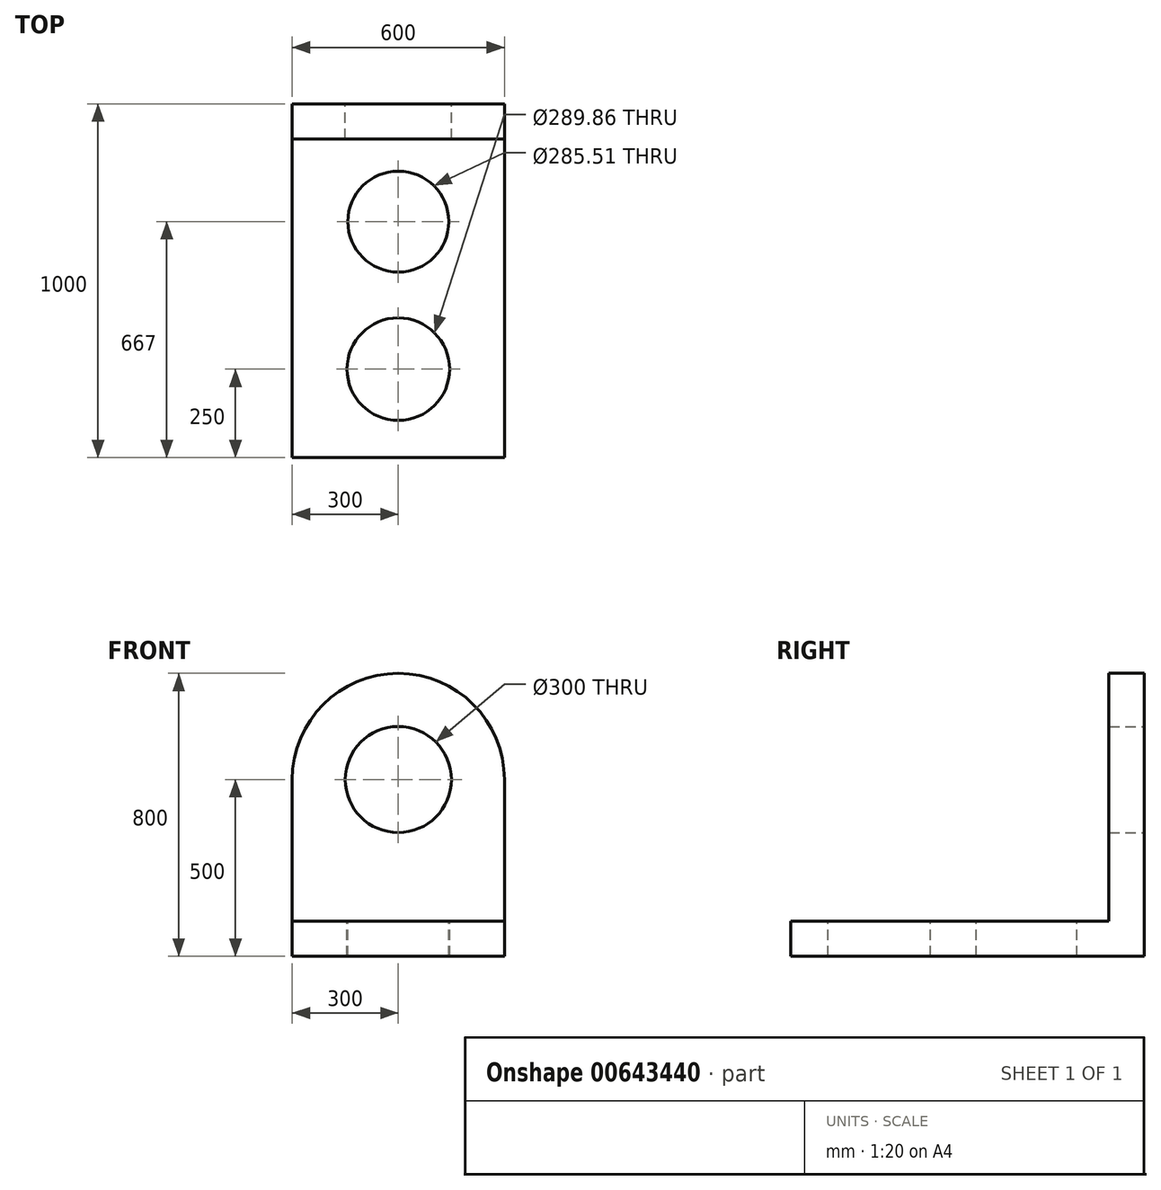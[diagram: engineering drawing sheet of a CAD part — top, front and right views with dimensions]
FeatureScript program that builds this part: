
annotation { "Feature Type Name" : "Feature", "Feature Type Description" : "" }
export const myFeature = defineFeature(function(context is Context, id is Id, definition is map)
    precondition{}
    {
        {
            var Q0;
            Q0=qCreatedBy(makeId("Front.planeOp"),FACE);
            var sketch = newSketch(context, id + "F0", { "sketchPlane" : qUnion([Q0])});
            skCircle(sketch, "E0", {"center": v(0, 0) * mm, "radius": 150 * mm});
            skArc(sketch, "E1", {"start": v(300, 0) * mm, "mid": v(0, 300) * mm, "end": v(-300, 0) * mm});
            skLineSegment(sketch, "E2", {"start": v(-300, 0) * mm, "end": v(-300, -500) * mm});
            skLineSegment(sketch, "E3", {"start": v(300, 0) * mm, "end": v(300, -500) * mm});
            skLineSegment(sketch, "E4", {"start": v(300, -500) * mm, "end": v(-300, -500) * mm});
            skLineSegment(sketch, "E5", {"start": v(-300, -400) * mm, "end": v(300, -400) * mm});
            skSolve(sketch);
        }
        {
            var Q0;
            Q0=makeQuery(id+"F0.imprint","IMPRINT",FACE,{"disambiguationData":[TD([[makeQuery(id+"F0.imprint","IMPRINT",EDGE,{"derivedFrom":sQuery(id+"F0.wireOp",EDGE,"E0")}),-1.0]])]});
            extrude(context, id + "F1", {"entities" : qUnion([Q0]), "depth" : 100 * mm, "offsetDistance" : 25 * mm});
        }
        {
            var Q0;
            {var subQ0=sQuery(id+"F0.wireOp",EDGE,"E4");Q0=makeQuery(id+"F0.imprint","IMPRINT",FACE,{"disambiguationData":[TD([[makeQuery(id+"F0.imprint","IMPRINT",EDGE,{"derivedFrom":subQ0}),-1.0]])]});}
            extrude(context, id + "F2", {"entities" : qUnion([Q0]), "operationType" : NewBodyOperationType.ADD, "depth" : 1000 * mm, "offsetDistance" : 25 * mm});
        }
        {
            var Q0;
            Q0=makeQuery(id+"F2.opExtrude","SWEPT_FACE",FACE,{"disambiguationData":[OSD([sQuery(id+"F0.wireOp",EDGE,"E5")])]});
            var sketch = newSketch(context, id + "F3", { "sketchPlane" : qUnion([Q0])});
            skCircle(sketch, "E6", {"center": v(0, -333) * mm, "radius": 142.76 * mm});
            skCircle(sketch, "E7", {"center": v(0, -750) * mm, "radius": 144.93 * mm});
            skSolve(sketch);
        }
        {
            var Q0;
            Q0=makeQuery(id+"F3.imprint","IMPRINT",FACE,{"disambiguationData":[TD([[makeQuery(id+"F3.imprint","IMPRINT",EDGE,{"derivedFrom":sQuery(id+"F3.wireOp",EDGE,"E6")}),1.0]])]});
            var Q1;
            Q1=makeQuery(id+"F3.imprint","IMPRINT",FACE,{"disambiguationData":[TD([[makeQuery(id+"F3.imprint","IMPRINT",EDGE,{"derivedFrom":sQuery(id+"F3.wireOp",EDGE,"E7")}),1.0]])]});
            extrude(context, id + "F4", {"entities" : qUnion([Q0, Q1]), "operationType" : NewBodyOperationType.REMOVE, "oppositeDirection" : true, "depth" : 100 * mm, "offsetDistance" : 25 * mm});
        }
    });
